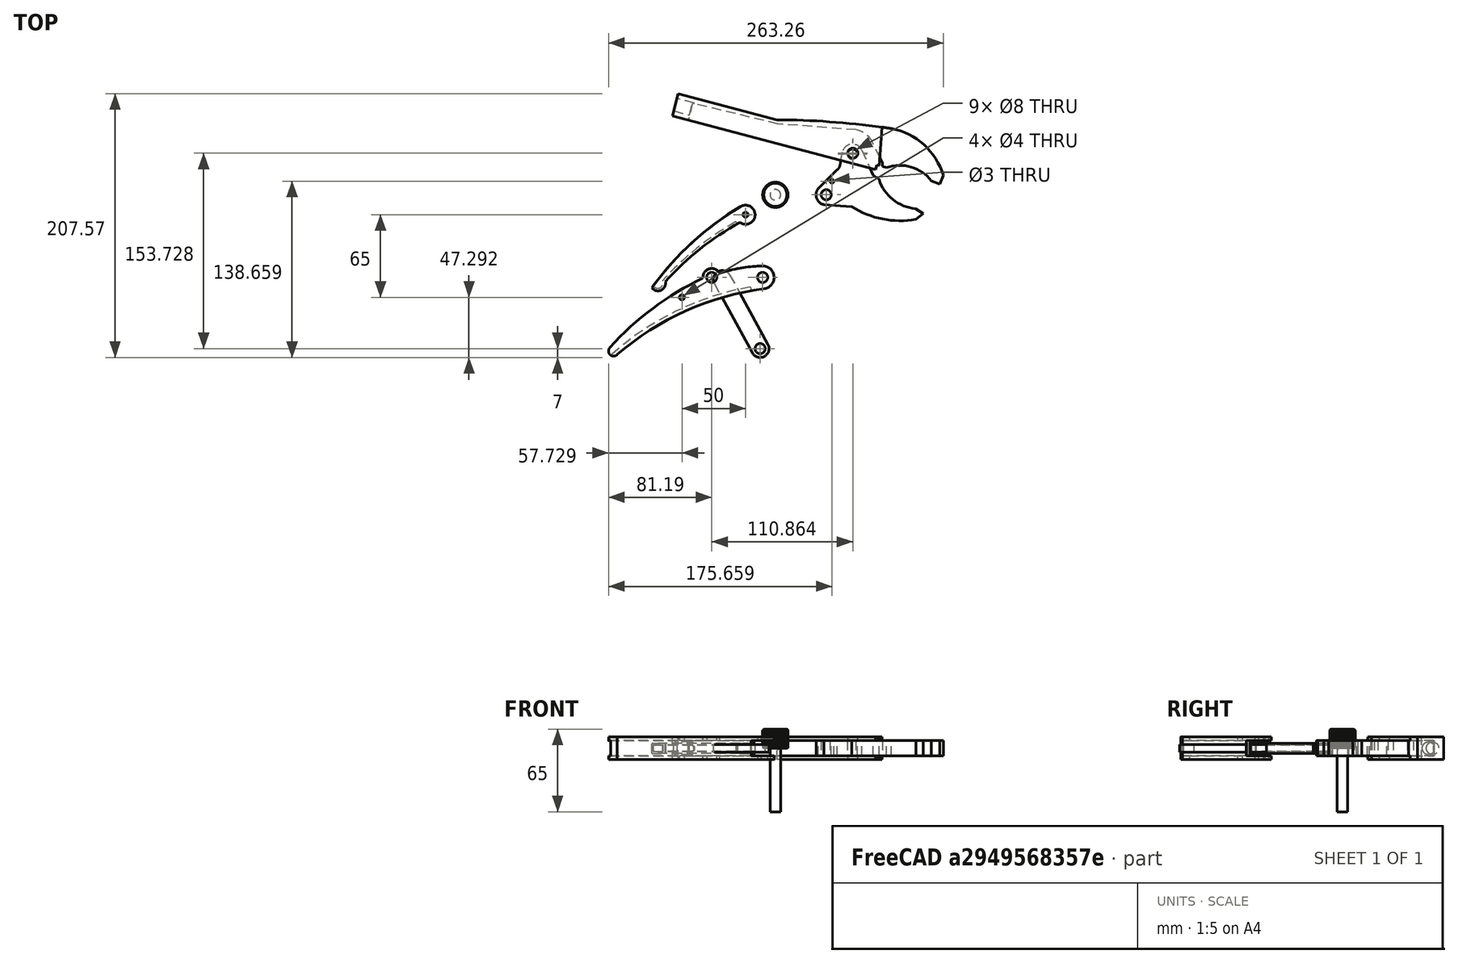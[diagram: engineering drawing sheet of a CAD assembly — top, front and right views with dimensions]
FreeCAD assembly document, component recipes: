
FREECAD ASSEMBLY — COMPONENT RECIPES ("pinza_a_scatto_assembly_4")

This assembly document has 7 components, labeled P0..P6 below (a component is one placed body or linked part). 6 of them carry a construction recipe — the FreeCAD feature program that regenerates the part from scratch, quoted from this document or its linked companion documents; the rest are supplied as boundary geometry only. No exploded tour is included for this assembly.
COMPONENT P0 — recipe-attached ("Body_leva", modeled in this document).
Construction recipe (the document's own serialized feature program — sketch geometry with constraints, then the solid features built on it; lengths are millimeters unless a unit is written):

FEATURE [Sketcher::SketchObject] Sketch
  MapMode = 5
  Support = -> [XY_Plane008]
  sketch-geometry (10):
    g0: ArcOfCircle CenterX=69.6412 CenterY=-227.074 CenterZ=0 NormalX=0 NormalY=0 NormalZ=1 AngleXU=0 Radius=220 StartAngle=1.7006 EndAngle=2.28427
    g1: ArcOfCircle CenterX=40 CenterY=0 CenterZ=0 NormalX=0 NormalY=0 NormalZ=1 AngleXU=0 Radius=9 StartAngle=4.84219 EndAngle=7.98378
    g2: Circle CenterX=40 CenterY=0 CenterZ=0 NormalX=0 NormalY=0 NormalZ=1 AngleXU=0 Radius=4
    g3: Circle CenterX=0 CenterY=0 CenterZ=0 NormalX=0 NormalY=0 NormalZ=1 AngleXU=0 Radius=4
    g4: Circle CenterX=-23.4606 CenterY=-15.7083 CenterZ=0 NormalX=0 NormalY=0 NormalZ=1 AngleXU=0 Radius=2
    g5: ArcOfCircle CenterX=-77.1869 CenterY=-57.9224 CenterZ=0 NormalX=0 NormalY=0 NormalZ=1 AngleXU=0 Radius=4 StartAngle=2.36265 EndAngle=5.50424
    g6: ArcOfCircle CenterX=0 CenterY=0 CenterZ=0 NormalX=0 NormalY=0 NormalZ=1 AngleXU=0 Radius=7 StartAngle=0.466872 EndAngle=3.24461
    g7: ArcOfCircle CenterX=91.1178 CenterY=-208.759 CenterZ=0 NormalX=0 NormalY=0 NormalZ=1 AngleXU=0 Radius=230 StartAngle=2.01135 EndAngle=2.41004
    g8: ArcOfCircle CenterX=40.8104 CenterY=-97.0573 CenterZ=0 NormalX=0 NormalY=0 NormalZ=1 AngleXU=0 Radius=106 StartAngle=1.58943 EndAngle=1.9029
    g9: LineSegment [constr] StartX=-80.0335 StartY=-55.1123 StartZ=0 EndX=-74.3402 EndY=-60.7325 EndZ=0
  constraints (24):
    c: Coincident(g1,g0)
    c: PointOnObject(g1,g-1)
    c: DistanceX(g1) = 40
    c: Coincident(g2,g1)
    c: Radius(g2) = 4
    c: Radius(g1) = 9
    c: Symmetric(g0,g1,g1)
    c: Coincident(g3,g-1)
    c: Radius(g3) = 4
    c: Coincident(g5,g0)
    c: Coincident(g6,g3)
    c: Coincident(g7,g5)
    c: Coincident(g7,g6)
    c: Coincident(g8,g6)
    c: Coincident(g8,g1)
    c: Radius(g6) = 7
    c: Radius(g4) = 2
    c: Radius(g0) = 220
    c: Radius(g7) = 230
    c: Radius(g8) = 106
    c: Radius(g5) = 4
    c: Coincident(g9,g5)
    c: Coincident(g9,g0)
    c: PointOnObject(g5,g9)
FEATURE [PartDesign::Pad] Pad
  Length = 18
  Length2 = 100
  Midplane = true
  Profile = -> Sketch
  Type = 0
FEATURE [Sketcher::SketchObject] Sketch001
  ExternalGeometry = -> [Sketch]
  MapMode = 5
  Support = -> [XY_Plane008]
  sketch-geometry (6):
    g0: ArcOfCircle CenterX=69.6412 CenterY=-227.074 CenterZ=0 NormalX=0 NormalY=0 NormalZ=1 AngleXU=0 Radius=223 StartAngle=1.74861 EndAngle=2.32723
    g1: ArcOfCircle CenterX=69.6412 CenterY=-227.074 CenterZ=0 NormalX=0 NormalY=0 NormalZ=1 AngleXU=0 Radius=247.987 StartAngle=1.65507 EndAngle=2.31653
    g2: LineSegment StartX=-98.6208 StartY=-44.9053 StartZ=0 EndX=-83.4106 EndY=-64.888 EndZ=0
    g3: LineSegment StartX=30.1969 StartY=-7.58974 StartZ=0 EndX=32.007 EndY=-14.7201 EndZ=0
    g4: LineSegment StartX=32.007 StartY=-14.7201 StartZ=0 EndX=56.0888 EndY=-10.6522 EndZ=0
    g5: LineSegment StartX=56.0888 StartY=-10.6522 StartZ=0 EndX=48.7666 EndY=20.033 EndZ=0
  constraints (10):
    c: Coincident(g0,g-3)
    c: Radius(g-3) = 220  'raggio_esterno'
    c: Radius(g0) = 223  'raggio_interno'
    c: Coincident(g1,g0)
    c: Coincident(g2,g1)
    c: Coincident(g2,g0)
    c: Coincident(g0,g3)
    c: Coincident(g3,g4)
    c: Coincident(g4,g5)
    c: Coincident(g5,g1)
FEATURE [PartDesign::Pocket] Pocket
  BaseFeature = -> Pad
  Length = 12
  Length2 = 100
  Midplane = true
  Profile = -> Sketch001
  Type = 0
FEATURE [PartDesign::Point] Point_2
  AttacherType = Attacher::AttachEnginePoint
  MapMode = 36
  Placement = pos=(40,0,0) rot=(1,0,0;1.5708rad)
  Support = -> [Sketch]
FEATURE [PartDesign::CoordinateSystem] LCS_3
  AttacherType = Attacher::AttachEngine3D
  MapMode = 11
  Placement = pos=(0,0,0) rot=(0,0,1;1.5708rad)
  Support = -> [Sketch,Point_2]
FEATURE [PartDesign::CoordinateSystem] LCS_4
  AttacherType = Attacher::AttachEngine3D
  MapMode = 11
  Placement = pos=(-23.4606,-15.7083,0) rot=(0,0,1;1.5708rad)
  Support = -> [Sketch]
FEATURE [PartDesign::Body] Body  label="Body_leva"
  Group = -> [Sketch,Pad,Sketch001,Pocket,LCS_3,Point_2,LCS_4]
  Origin = -> Origin008
  Placement = pos=(-50,-65,0) rot=(0,0,1;0rad)
  Tip = -> Pocket
COMPONENT P1 — recipe-attached ("Body_leva_sgancio", modeled in this document).
Construction recipe (the document's own serialized feature program — sketch geometry with constraints, then the solid features built on it; lengths are millimeters unless a unit is written):

FEATURE [PartDesign::SubShapeBinder] Binder
  BindMode = 0
  ClaimChildren = false
  Context = -> Body001 [Binder.]
  Fuse = false
  MakeFace = true
  PartialLoad = false
  Relative = true
  Support = -> [Body[Pocket.Face8]]
  _Version = 2
FEATURE [Sketcher::SketchObject] Sketch002
  ExternalGeometry = -> [Binder]
  MapMode = 5
  Support = -> [XY_Plane001]
  sketch-geometry (5):
    g0: ArcOfCircle CenterX=79.0589 CenterY=-216.254 CenterZ=0 NormalX=0 NormalY=0 NormalZ=1 AngleXU=0 Radius=222 StartAngle=2.07369 EndAngle=2.41241
    g1: ArcOfCircle CenterX=91.1178 CenterY=-208.759 CenterZ=0 NormalX=0 NormalY=0 NormalZ=1 AngleXU=0 Radius=232 StartAngle=2.10721 EndAngle=2.51758
    g2: ArcOfCircle CenterX=-23.4606 CenterY=-15.7083 CenterZ=0 NormalX=0 NormalY=0 NormalZ=1 AngleXU=0 Radius=7.51 StartAngle=4.0739 EndAngle=8.4135
    g3: ArcOfCircle CenterX=-92.3563 CenterY=-69.6072 CenterZ=0 NormalX=0 NormalY=0 NormalZ=1 AngleXU=0 Radius=6 StartAngle=3.7841 EndAngle=6.49533
    g4: Circle CenterX=-23.4606 CenterY=-15.7083 CenterZ=0 NormalX=0 NormalY=0 NormalZ=1 AngleXU=0 Radius=2
  constraints (11):
    c: Coincident(g2,g0)
    c: Coincident(g2,g1)
    c: Coincident(g3,g1)
    c: Coincident(g3,g0)
    c: Radius(g1) = 232
    c: Radius(g0) = 222
    c: DistanceX(g0) = 79.0589
    c: DistanceY(g0) = -216.254
    c: Coincident(g4,g2)
    c: Radius(g2) = 7.51
    c: Radius(g3) = 6
FEATURE [PartDesign::Pad] Pad001
  Length = 8
  Length2 = 100
  Midplane = true
  Profile = -> Sketch002
  Type = 0
FEATURE [Sketcher::SketchObject] Sketch003
  ExternalGeometry = -> [Sketch002]
  MapMode = 5
  Support = -> [XY_Plane001]
  sketch-geometry (6):
    g0: ArcOfCircle CenterX=79.0589 CenterY=-216.254 CenterZ=0 NormalX=0 NormalY=0 NormalZ=1 AngleXU=0 Radius=224 StartAngle=2.08534 EndAngle=2.41757
    g1: ArcOfCircle CenterX=91.1178 CenterY=-208.759 CenterZ=0 NormalX=0 NormalY=0 NormalZ=1 AngleXU=0 Radius=234 StartAngle=2.10628 EndAngle=2.48715
    g2: ArcOfCircle CenterX=-23.4606 CenterY=-15.7083 CenterZ=0 NormalX=0 NormalY=0 NormalZ=1 AngleXU=0 Radius=9.50799 StartAngle=3.76488 EndAngle=8.38589
    g3: ArcOfCircle CenterX=-92.3563 CenterY=-69.6072 CenterZ=0 NormalX=0 NormalY=0 NormalZ=1 AngleXU=0 Radius=4 StartAngle=3.94525 EndAngle=6.73088
    g4: LineSegment StartX=-95.1326 StartY=-72.4868 StartZ=0 EndX=-97.2926 EndY=-70.4044 EndZ=0
    g5: LineSegment StartX=-97.2926 StartY=-70.4044 StartZ=0 EndX=-94.5353 EndY=-66.3195 EndZ=0
  constraints (13):
    c: Coincident(g0,g-3)
    c: Radius(g0) = 224
    c: Coincident(g1,g-6)
    c: Radius(g1) = 234
    c: Coincident(g2,g-4)
    c: Coincident(g2,g1)
    c: Coincident(g0,g2)
    c: Coincident(g3,g-5)
    c: Radius(g3) = 4
    c: Coincident(g0,g3)
    c: Tangent(g3,g4) = 1.5708
    c: Coincident(g4,g5)
    c: Coincident(g5,g1)
FEATURE [PartDesign::Pocket] Pocket001
  BaseFeature = -> Pad001
  Length = 5
  Length2 = 100
  Midplane = true
  Profile = -> Sketch003
  Type = 0
FEATURE [PartDesign::CoordinateSystem] LCS_5
  AttacherType = Attacher::AttachEngine3D
  MapMode = 11
  Placement = pos=(-23.4606,-15.7083,0) rot=(0,0,1;1.5708rad)
  Support = -> [Sketch002]
FEATURE [PartDesign::Body] Body001  label="Body_leva_sgancio"
  Group = -> [Sketch002,Binder,Pad001,Sketch003,Pocket001,LCS_5]
  Origin = -> Origin001
  Tip = -> Pocket001
COMPONENT P2 — recipe-attached ("Body_pinza_free", modeled in this document).
Construction recipe (the document's own serialized feature program — sketch geometry with constraints, then the solid features built on it; lengths are millimeters unless a unit is written):

FEATURE [Sketcher::SketchObject] Sketch004
  MapMode = 5
  Support = -> [XY_Plane002]
  sketch-geometry (16):
    g0: Circle CenterX=60.6264 CenterY=31.9148 CenterZ=0 NormalX=0 NormalY=0 NormalZ=1 AngleXU=0 Radius=4
    g1: LineSegment [constr] StartX=40 StartY=0 StartZ=0 EndX=60.6264 EndY=31.9148 EndZ=0
    g2: Circle CenterX=44.4687 CenterY=10.6594 CenterZ=0 NormalX=0 NormalY=0 NormalZ=1 AngleXU=0 Radius=1.5
    g3: LineSegment StartX=116.148 StartY=-14.7672 StartZ=0 EndX=110.433 EndY=-19.3215 EndZ=0
    g4: ArcOfCircle CenterX=40 CenterY=0 CenterZ=0 NormalX=0 NormalY=0 NormalZ=1 AngleXU=0 Radius=8 StartAngle=2.46455 EndAngle=4.45899
    g5: LineSegment StartX=50.7819 StartY=23.2474 StartZ=0 EndX=52.7748 EndY=33.4487 EndZ=0
    g6: ArcOfCircle CenterX=60.6264 CenterY=31.9148 CenterZ=0 NormalX=0 NormalY=0 NormalZ=1 AngleXU=0 Radius=8 StartAngle=0.388483 EndAngle=2.94866
    g7: LineSegment StartX=68.0302 StartY=34.9451 StartZ=0 EndX=76.7936 EndY=15.4999 EndZ=0
    g8: LineSegment StartX=76.7936 StartY=15.4999 StartZ=0 EndX=81.5427 EndY=12.1782 EndZ=0
    g9: ArcOfCircle CenterX=44.8932 CenterY=24.3978 CenterZ=0 NormalX=0 NormalY=0 NormalZ=1 AngleXU=0 Radius=6 StartAngle=5.40857 EndAngle=6.09025
    g10: LineSegment StartX=37.9944 StartY=-7.74453 StartZ=0 EndX=60.1114 EndY=-9.24796 EndZ=0
    g11: ArcOfCircle CenterX=98.05 CenterY=49.546 CenterZ=0 NormalX=0 NormalY=0 NormalZ=1 AngleXU=0 Radius=69.9719 StartAngle=4.13934 EndAngle=4.89029
    g12: LineSegment StartX=116.148 StartY=-14.7672 StartZ=0 EndX=110.27 EndY=-10.8789 EndZ=0
    g13: ArcOfCircle CenterX=112.96 CenterY=21.897 CenterZ=0 NormalX=0 NormalY=0 NormalZ=1 AngleXU=0 Radius=32.8861 StartAngle=3.4416 EndAngle=4.6305
    g14: Circle CenterX=40 CenterY=0 CenterZ=0 NormalX=0 NormalY=0 NormalZ=1 AngleXU=0 Radius=4
    g15: LineSegment StartX=33.7646 StartY=5.01195 StartZ=0 EndX=48.7409 EndY=19.794 EndZ=0
  constraints (2):
    c: Coincident(g13,g12)
    c: Coincident(g13,g8)
FEATURE [PartDesign::Pad] Pad002
  Length = 12
  Length2 = 100
  Midplane = true
  Profile = -> Sketch004
  Type = 0
FEATURE [PartDesign::Point] Point_1
  AttacherType = Attacher::AttachEnginePoint
  MapMode = 36
  Placement = pos=(60.6264,31.9148,0) rot=(1,0,0;1.5708rad)
  Support = -> [Sketch004]
FEATURE [PartDesign::CoordinateSystem] LCS_2
  AttacherType = Attacher::AttachEngine3D
  MapMode = 11
  Placement = pos=(40,0,0) rot=(0,0,1;2.56783rad)
  Support = -> [Sketch004,Point_1]
FEATURE [PartDesign::Body] Body002  label="Body_pinza_free"
  Group = -> [Sketch004,Pad002,LCS_2,Point_1]
  Origin = -> Origin002
  Tip = -> Pad002
COMPONENT P3 — recipe-attached ("Body_block", modeled in this document).
Construction recipe (the document's own serialized feature program — sketch geometry with constraints, then the solid features built on it; lengths are millimeters unless a unit is written):

FEATURE [Sketcher::SketchObject] Sketch008
  MapMode = 5
  Support = -> [XY_Plane004]
  sketch-geometry (7):
    g0: LineSegment StartX=84.054 StartY=25.0066 StartZ=0 EndX=76.6129 EndY=40.9426 EndZ=0
    g1: ArcOfCircle CenterX=60.1999 CenterY=33.2788 CenterZ=0 NormalX=0 NormalY=0 NormalZ=1 AngleXU=0 Radius=18.1141 StartAngle=0.436851 EndAngle=1.39859
    g2: LineSegment StartX=63.3038 StartY=51.125 StartZ=0 EndX=2.08825 EndY=55.7684 EndZ=0
    g3: LineSegment StartX=2.08825 StartY=55.7684 StartZ=0 EndX=-65.344 EndY=72.0326 EndZ=0
    g4: LineSegment StartX=-65.344 StartY=72.0326 StartZ=0 EndX=-69.7298 EndY=53.7583 EndZ=0
    g5: LineSegment StartX=-69.7298 StartY=53.7583 StartZ=0 EndX=84.054 EndY=17.9406 EndZ=0
    g6: LineSegment StartX=84.054 StartY=17.9406 StartZ=0 EndX=84.054 EndY=25.0066 EndZ=0
  constraints (8):
    c: Tangent(g0,g1) = -1.5708
    c: Coincident(g1,g2)
    c: Coincident(g2,g3)
    c: Coincident(g3,g4)
    c: Coincident(g4,g5)
    c: Coincident(g5,g6)
    c: Coincident(g6,g0)
    c: Vertical(g6)
FEATURE [Sketcher::SketchObject] Sketch007
  AttachmentOffset = pos=(0,0,6) rot=(0,0,1;0rad)
  MapMode = 5
  Placement = pos=(0,0,6) rot=(0,0,1;0rad)
  Support = -> [XY_Plane004]
  sketch-geometry (5):
    g0: LineSegment StartX=81.6339 StartY=20.9875 StartZ=0 EndX=84.0187 EndY=54.6693 EndZ=0
    g1: LineSegment StartX=84.0187 StartY=54.6693 StartZ=0 EndX=91.8155 EndY=53.6255 EndZ=0
    g2: ArcOfCircle CenterX=85.2659 CenterY=4.70524 CenterZ=0 NormalX=0 NormalY=0 NormalZ=1 AngleXU=0 Radius=49.3567 StartAngle=0.206087 EndAngle=1.4377
    g3: LineSegment StartX=133.578 StartY=14.8052 StartZ=0 EndX=129.18 EndY=5.66002 EndZ=0
    g4: LineSegment StartX=129.18 StartY=5.66002 StartZ=0 EndX=81.6339 EndY=20.9875 EndZ=0
  constraints (5):
    c: Coincident(g0,g1)
    c: Tangent(g1,g2) = 1.5708
    c: Coincident(g2,g3)
    c: Coincident(g3,g4)
    c: Coincident(g4,g0)
FEATURE [PartDesign::SubShapeBinder] Binder002
  BindMode = 0
  ClaimChildren = false
  Context = -> Body004 [Binder002.]
  Fuse = false
  MakeFace = true
  PartialLoad = false
  Relative = true
  Support = -> [Body002[Pad002.Face17]]
  _Version = 2
FEATURE [Sketcher::SketchObject] Sketch005
  ExternalGeometry = -> [Binder002]
  MapMode = 5
  Support = -> [XY_Plane004]
  sketch-geometry (12):
    g0: LineSegment StartX=129.192 StartY=8.29089 StartZ=0 EndX=132.069 EndY=15.2632 EndZ=0
    g1: LineSegment StartX=-76.4002 StartY=79.57 StartZ=0 EndX=-81.0038 EndY=62.1687 EndZ=0
    g2: LineSegment StartX=-81.0038 StartY=62.1687 StartZ=0 EndX=78.7729 EndY=19.8989 EndZ=0
    g3: ArcOfCircle CenterX=81.0345 CenterY=-0.176411 CenterZ=0 NormalX=0 NormalY=0 NormalZ=1 AngleXU=0 Radius=53.319 StartAngle=0.293779 EndAngle=1.37856
    g4: LineSegment StartX=129.192 StartY=8.29089 StartZ=0 EndX=122.692 EndY=10.9049 EndZ=0
    g5: LineSegment StartX=78.7729 StartY=19.8989 StartZ=0 EndX=79.7012 EndY=23.4161 EndZ=0
    g6: LineSegment StartX=79.7012 StartY=23.4161 StartZ=0 EndX=87.416 EndY=21.3159 EndZ=0
    g7: ArcOfCircle CenterX=97.9281 CenterY=-8.03417 CenterZ=0 NormalX=0 NormalY=0 NormalZ=1 AngleXU=0 Radius=31.1758 StartAngle=0.6529 EndAngle=1.91472
    g8: LineSegment StartX=-76.4002 StartY=79.57 StartZ=0 EndX=1.21394 EndY=59.0368 EndZ=0
    g9: ArcOfCircle CenterX=-2.92778 CenterY=-587.68 CenterZ=0 NormalX=0 NormalY=0 NormalZ=1 AngleXU=0 Radius=646.73 StartAngle=1.4247 EndAngle=1.56439
    g10: Circle CenterX=60.8645 CenterY=32.7279 CenterZ=0 NormalX=0 NormalY=0 NormalZ=1 AngleXU=0 Radius=4
    g11: LineSegment [constr] StartX=87.416 StartY=21.3159 StartZ=0 EndX=81.5427 EndY=12.1782 EndZ=0
  constraints (22):
    c: Coincident(g1,g2)
    c: Coincident(g3,g0)
    c: Coincident(g0,g4)
    c: Coincident(g5,g6)
    c: Coincident(g7,g6)
    c: Coincident(g7,g4)
    c: DistanceX(g0) = 132.069
    c: DistanceY(g0) = 15.2632
    c: Distance(g1) = 18
    c: Perpendicular(g1,g2)
    c: Coincident(g2,g5)
    c: Coincident(g8,g1)
    c: Coincident(g9,g8)
    c: Coincident(g9,g3)
    c: Perpendicular(g1,g8)
    c: DistanceX(g2) = 78.7729
    c: DistanceX(g8) = 1.21394
    c: DistanceY(g8) = 59.0368
    c: Coincident(g11,g6)
    c: Coincident(g11,g-3)
    c: DistanceX(g6) = 87.416
    c: DistanceY(g6) = 21.3159
FEATURE [PartDesign::Plane] DatumPlane
  AttachmentOffset = pos=(0,0,0) rot=(0,1,0;1.5708rad)
  Length = 173.227
  MapMode = 7
  Placement = pos=(-76.4002,79.57,0) rot=(-0.478114,0.62105,0.62105;4.03357rad)
  ResizeMode = 0
  Support = -> [Sketch005]
  Width = 67.6401
FEATURE [Sketcher::SketchObject] Sketch009
  ExternalGeometry = -> [Sketch005]
  MapMode = 5
  Placement = pos=(-76.4002,79.57,0) rot=(-0.478114,0.62105,0.62105;4.03357rad)
  Support = -> [DatumPlane]
  sketch-geometry (1):
    g0: Circle CenterX=9 CenterY=7.1e-15 CenterZ=0 NormalX=0 NormalY=0 NormalZ=1 AngleXU=0 Radius=5
  constraints (1):
    c: Radius(g0) = 5
FEATURE [PartDesign::Pad] Pad003
  Length = 18
  Length2 = 100
  Midplane = true
  Profile = -> Sketch005
  Type = 0
FEATURE [PartDesign::Pocket] Pocket002
  BaseFeature = -> Pad003
  Length = 4
  Length2 = 100
  Profile = -> Sketch007
  Reversed = true
  Type = 1
FEATURE [PartDesign::Mirrored] Mirrored
  BaseFeature = -> Pocket002
  MirrorPlane = -> XY_Plane004
  Originals = -> [Pocket002]
FEATURE [PartDesign::Pocket] Pocket003
  BaseFeature = -> Mirrored
  Length = 12
  Length2 = 100
  Midplane = true
  Profile = -> Sketch008
  Type = 0
FEATURE [PartDesign::Pocket] Pocket004
  BaseFeature = -> Pocket003
  Length = 14
  Length2 = 100
  Profile = -> Sketch009
  Type = 0
FEATURE [PartDesign::CoordinateSystem] LCS_1
  AttacherType = Attacher::AttachEngine3D
  AttachmentOffset = pos=(0,0,0) rot=(0,0,1;-0.256563rad)
  MapMode = 11
  Placement = pos=(60.8645,32.7279,0) rot=(0,0,-1;4.96895rad)
  Support = -> [Sketch005]
FEATURE [PartDesign::CoordinateSystem] LCS_9
  AttacherType = Attacher::AttachEngine3D
  MapMode = 11
  Placement = pos=(-78.702,70.8693,7.1e-15) rot=(-0.127896,-0.983507,-0.127896;1.58743rad)
  Support = -> [Pocket004]
FEATURE [PartDesign::Body] Body004  label="Body_block"
  Group = -> [Sketch005,Binder002,Pad003,Sketch007,Pocket002,Mirrored,Sketch008,Pocket003,Sketch009,Pocket004,DatumPlane,LCS_1,LCS_9]
  Origin = -> Origin004
  Tip = -> Pocket004
COMPONENT P4 — recipe-attached ("Body_staffa", modeled in this document).
Construction recipe (the document's own serialized feature program — sketch geometry with constraints, then the solid features built on it; lengths are millimeters unless a unit is written):

FEATURE [PartDesign::SubShapeBinder] Binder003
  BindMode = 0
  ClaimChildren = false
  Context = -> Body005 [Binder003.]
  Fuse = false
  MakeFace = true
  PartialLoad = false
  Relative = true
  Support = -> [Body[Pocket.Face14]]
  _Version = 2
FEATURE [Sketcher::SketchObject] Sketch006
  ExternalGeometry = -> [Binder003]
  MapMode = 5
  Support = -> [XY_Plane005]
  sketch-geometry (5):
    g0: Circle CenterX=0 CenterY=0 CenterZ=0 NormalX=0 NormalY=0 NormalZ=1 AngleXU=0 Radius=4
    g1: ArcOfCircle CenterX=-29.8277 CenterY=54.3536 CenterZ=0 NormalX=0 NormalY=0 NormalZ=1 AngleXU=0 Radius=7 StartAngle=0.501899 EndAngle=3.64349
    g2: ArcOfCircle CenterX=0 CenterY=0 CenterZ=0 NormalX=0 NormalY=0 NormalZ=1 AngleXU=0 Radius=7 StartAngle=3.64349 EndAngle=6.78508
    g3: LineSegment StartX=-35.9644 StartY=50.9859 StartZ=0 EndX=-6.13669 EndY=-3.36764 EndZ=0
    g4: LineSegment StartX=-23.691 StartY=57.7212 StartZ=0 EndX=6.13669 EndY=3.36764 EndZ=0
  constraints (11):
    c: Coincident(g0,g-1)
    c: Equal(g0,g-3)
    c: Tangent(g1,g4) = 1.5708
    c: Tangent(g1,g3) = -1.5708
    c: Tangent(g3,g2) = -1.5708
    c: Tangent(g4,g2) = 1.5708
    c: Equal(g1,g2)
    c: Coincident(g2,g0)
    c: Radius(g2) = 7
    c: Distance(g0,g1) = 62
    c: DistanceX(g1) = -29.8277
FEATURE [PartDesign::Pad] Pad004
  Length = 6
  Length2 = 100
  Midplane = true
  Profile = -> Sketch006
  Type = 0
FEATURE [PartDesign::Point] Point_3
  AttacherType = Attacher::AttachEnginePoint
  MapMode = 36
  Placement = pos=(-29.8277,54.3536,3) rot=(0.940124,0.241004,0.241004;1.6325rad)
  Support = -> [Pad004]
FEATURE [PartDesign::CoordinateSystem] LCS_6
  AttacherType = Attacher::AttachEngine3D
  MapMode = 11
  Placement = pos=(0,0,3) rot=(0,0,1;3.64349rad)
  Support = -> [Pad004,Point_3]
FEATURE [PartDesign::Body] Body005  label="Body_staffa"
  Group = -> [Sketch006,Binder003,Pad004,Point_3,LCS_6]
  Origin = -> Origin005
  Placement = pos=(-12,-121,0) rot=(0,0,1;0rad)
  Tip = -> Pad004
COMPONENT P5 — recipe-attached ("Body_vite_regolazione", modeled in this document).
Construction recipe (the document's own serialized feature program — sketch geometry with constraints, then the solid features built on it; lengths are millimeters unless a unit is written):

FEATURE [Sketcher::SketchObject] Sketch012
  MapMode = 5
  Support = -> [XY_Plane007]
  sketch-geometry (4):
    g0: LineSegment StartX=-0.5 StartY=10.5 StartZ=0 EndX=-0.05 EndY=9.5 EndZ=0
    g1: LineSegment StartX=-0.05 StartY=9.5 StartZ=0 EndX=0.05 EndY=9.5 EndZ=0
    g2: LineSegment StartX=0.05 StartY=9.5 StartZ=0 EndX=0.5 EndY=10.5 EndZ=0
    g3: LineSegment StartX=0.5 StartY=10.5 StartZ=0 EndX=-0.5 EndY=10.5 EndZ=0
  constraints (10):
    c: Coincident(g0,g1)
    c: Coincident(g1,g2)
    c: Coincident(g2,g3)
    c: Coincident(g3,g0)
    c: Symmetric(g0,g2,g-2)
    c: Symmetric(g1,g0,g-2)
    c: DistanceY(g-1,g1) = 9.5
    c: DistanceX(g3,g3) = 1
    c: DistanceY(g1,g2) = 1
    c: Distance(g1) = 0.1
FEATURE [Sketcher::SketchObject] Sketch013
  MapMode = 5
  Placement = pos=(0,0,0) rot=(1,0,0;1.5708rad)
  Support = -> [XZ_Plane007]
  sketch-geometry (7):
    g0: LineSegment StartX=-10.3 StartY=-0.45 StartZ=0 EndX=-8.8 EndY=-0.45 EndZ=0
    g1: LineSegment StartX=-8.8 StartY=-0.45 StartZ=0 EndX=-10.3 EndY=1.05 EndZ=0
    g2: LineSegment StartX=-10.3 StartY=1.05 StartZ=0 EndX=-10.3 EndY=-0.45 EndZ=0
    g3: LineSegment [constr] StartX=-10.3 StartY=-0.45 StartZ=0 EndX=-10.3 EndY=15.3 EndZ=0
    g4: LineSegment StartX=-10.3 StartY=15.3 StartZ=0 EndX=-10.3 EndY=13.8 EndZ=0
    g5: LineSegment StartX=-10.3 StartY=13.8 StartZ=0 EndX=-8.8 EndY=15.3 EndZ=0
    g6: LineSegment StartX=-8.8 StartY=15.3 StartZ=0 EndX=-10.3 EndY=15.3 EndZ=0
  constraints (20):
    c: Coincident(g0,g1)
    c: Coincident(g1,g2)
    c: Coincident(g2,g0)
    c: Perpendicular(g2,g0)
    c: Parallel(g0,g-1)
    c: Equal(g0,g2)
    c: DistanceX(g0) = -10.3
    c: DistanceY(g0) = -0.45
    c: Coincident(g3,g0)
    c: Vertical(g3)
    c: DistanceY(g2,g2) = 1.5
    c: Coincident(g3,g4)
    c: Vertical(g4)
    c: Coincident(g4,g5)
    c: Coincident(g5,g6)
    c: Coincident(g6,g4)
    c: Horizontal(g6)
    c: Equal(g6,g4)
    c: DistanceX(g6,g6) = 1.5
    c: Distance(g3) = 15.75
FEATURE [Sketcher::SketchObject] Sketch011
  MapMode = 5
  Support = -> [XY_Plane007]
  sketch-geometry (1):
    g0: Circle CenterX=0 CenterY=0 CenterZ=0 NormalX=0 NormalY=0 NormalZ=1 AngleXU=0 Radius=10
  constraints (2):
    c: Coincident(g0,g-1)
    c: Radius(g0) = 10
FEATURE [PartDesign::FeatureBase] BaseFeature
  BaseFeature = -> ScrewTap
FEATURE [PartDesign::Pad] Pad005
  BaseFeature = -> BaseFeature
  Length = 15
  Length2 = 100
  Profile = -> Sketch011
  Type = 0
FEATURE [PartDesign::Groove] Groove
  Angle = 360
  Axis = (0,-2e-16,1)
  Base = (0,0,0)
  BaseFeature = -> Pad005
  Profile = -> Sketch013
  ReferenceAxis = -> Sketch013 [V_Axis]
  Reversed = true
FEATURE [PartDesign::Pocket] Pocket005
  BaseFeature = -> Groove
  Length = 5
  Length2 = 100
  Profile = -> Sketch012
  Reversed = true
  Type = 1
FEATURE [PartDesign::PolarPattern] PolarPattern
  Angle = 360
  Axis = -> Sketch012 [N_Axis]
  BaseFeature = -> Pocket005
  Occurrences = 40
  Originals = -> [Pocket005]
FEATURE [PartDesign::CoordinateSystem] LCS_8
  AttacherType = Attacher::AttachEngine3D
  MapMode = 11
  Placement = pos=(0,0,-50) rot=(0,0,1;1.5708rad)
  Support = -> [PolarPattern]
FEATURE [PartDesign::Body] Body007  label="Body_vite_regolazione"
  BaseFeature = -> ScrewTap
  Group = -> [BaseFeature,Sketch011,Pad005,Sketch012,Sketch013,Groove,Pocket005,PolarPattern,LCS_8]
  Origin = -> Origin007
  Tip = -> PolarPattern
COMPONENT P6 — geometry summary ("Model"; no construction recipe available for this part):
  bounding box: 240.0 x 112.3 x 20.0 mm
  tessellated surface: 15,082 triangles
  volume: 105433 mm^3 (20% of its bounding box)
  symmetry: mirror-symmetric across its z mid-plane
PROVENANCE & LICENSES
A FreeCAD (.FCStd) document from a public repository crawl; recipes are the document's own serialized feature recipes (and, for linked parts, companion documents' recipes).
License: gpl-3.0.
